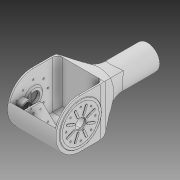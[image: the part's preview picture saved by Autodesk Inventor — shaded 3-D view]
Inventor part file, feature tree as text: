
AUTODESK INVENTOR PART (.ipt)
format: ipt  version: 2020 (Build 240168000, 168)  size: 957,952 bytes
history: native  units: mm
features: sketch x33, extrude x29, projected_geometry x8, plane x6, chamfer x3, fillet x3, pattern_circular x2, revolve x2, loft x2, other x2
ambient origin geometry x8: Origin, YZ Plane, XZ Plane, XY Plane, X Axis, Y Axis, Z Axis, Center Point
bodies: Solid1 (feature_tree)
feature tree (90):
  extrude  "Extrusion1"  Depth=250.0mm
  extrude  "Extrusion2"  Depth=100.0mm TaperAngle=0.0deg
  extrude  "Extrusion3"  TaperAngle=0.0deg  [1 undecoded]
  extrude  "Extrusion4"  Depth=10.0mm
  extrude  "Extrusion5"  Depth=30.0mm
  pattern_circular  "Circular Pattern1"  Count=8 Angle=360.0deg
  plane  "Work Plane1"
  plane  "Work Plane2"
  extrude  "Extrusion6"  Depth=30.0mm
  extrude  "Extrusion7"  Depth=2.0mm
  extrude  "Extrusion8"  Depth=2.0mm
  extrude  "Extrusion9"  [1 undecoded]
  chamfer  "Chamfer1"  Distance=10.0mm
  extrude  "Extrusion13"  Depth=10.0mm TaperAngle=0.0deg
  extrude  "Extrusion14"  Depth=3.0mm TaperAngle=0.0deg
  extrude  "Extrusion15"  Depth=95.1mm
  extrude  "Extrusion16"  Depth=10.0mm
  extrude  "Extrusion17"  Depth=80.0mm
  extrude  "Extrusion18"  Depth=60.0mm
  extrude  "Extrusion19"  Depth=80.0mm TaperAngle=360.0deg
  extrude  "Extrusion20"  Depth=15.5mm TaperAngle=0.0deg
  fillet  "Fillet2"  Radius=22.1mm
  pattern_circular  "Circular Pattern2"  Count=8 Angle=360.0deg
  extrude  "Extrusion22"  Depth=10.0mm
  plane  "Work Plane3"
  revolve  "Revolution1"  [1 undecoded]
  revolve  "Revolution2"  [1 undecoded]
  plane  "Work Plane4"
  extrude  "Extrusion23"  Depth=5.2mm
  extrude  "Extrusion24"  Depth=5.0mm
  fillet  "Fillet3"  Radius=5.2mm
  loft  "Loft1"
  extrude  "Extrusion25"  Depth=10.0mm
  extrude  "Extrusion26"  Depth=10.0mm
  extrude  "Extrusion27"  Depth=10.0mm
  extrude  "Extrusion28"  Depth=10.0mm
  plane  "Work Plane5"
  extrude  "Extrusion29"  Depth=10.0mm
  extrude  "Extrusion30"  Depth=10.0mm TaperAngle=0.0deg
  extrude  "Extrusion31"  Depth=10.0mm
  sketch  "Sketch38"  dims[d109=2.5mm d110=5.2mm]
  plane  "Work Plane6"
  extrude  "Extrusion33"  Depth=10.0mm TaperAngle=0.0deg
  loft  "Loft2"
  fillet  "Fillet5"  Radius=10.0mm
  chamfer  "Chamfer4"  Distance=18.8mm
  extrude  "Extrusion34"  Depth=10.0mm TaperAngle=0.0deg
  chamfer  "Chamfer5"  Distance=6.0mm
  sketch  "Sketch1"  dims[d0=50.0mm d1=250.0mm]
  sketch  "Sketch2"  dims[d2=50.0mm d3=100.0mm d4=0.0mm]
  sketch  "Sketch4"  dims[d5=5.0mm d7=0.0mm d8=0.0mm]
  sketch  "Sketch5"  dims[d11=10.0mm d12=0.0mm d14=85.0mm]
  sketch  "Sketch7"  dims[d15=1.0mm d16=0.0mm d17=30.0mm]
  projected_geometry  "Projected Loop1"
  sketch  "Sketch8"  dims[d18=3.3mm]
  projected_geometry  "Projected Loop2"
  projected_geometry  "Projected Loop4"
  sketch  "Sketch9"  dims[d19=15.0mm d20=0.0mm d21=80.0mm d22=360.0deg]
  sketch  "Sketch10"  dims[d24=30.0mm d25=30.0mm]
  sketch  "Sketch14"  dims[d30=-3.0mm d31=2.0mm]
  sketch  "Sketch15"  dims[d32=2.0mm d33=2.0mm]
  sketch  "Sketch16"  dims[d34=31.5mm d35=0.0mm d36=-5.0mm d38=10.0mm d39=0.0mm]
  sketch  "Sketch17"  dims[d40=22.1mm d41=10.0mm d42=0.0mm]
  sketch  "Sketch18"  dims[d43=5.0mm d44=3.0mm d45=0.0mm]
  sketch  "Sketch19"  dims[d56=3.0mm d57=2.0mm d58=45.0deg d62=95.1mm]
  sketch  "Sketch20"  dims[d63=10.0mm d64=0.0mm d65=3.0mm]
  sketch  "Sketch21"  dims[d66=0.5mm d67=0.0mm d68=80.0mm]
  sketch  "Sketch23"  dims[d69=15.5mm d70=0.0mm d71=60.0mm]
  other  "Work Axis1"
  sketch  "Sketch24"  dims[d72=3.2mm d73=80.0mm d75=360.0deg]
  sketch  "Sketch25"  dims[d77=15.5mm d78=0.0mm d79=15.5mm d80=0.0mm d81=22.1mm]
  projected_geometry  "Projected Loop5"
  projected_geometry  "Projected Loop6"
  sketch  "Sketch26"  dims[d82=0.0mm d83=0.0mm]
  sketch  "Sketch27"  dims[d84=76.0mm]
  sketch  "Sketch28"  dims[d85=0.1mm d86=0.0mm]
  sketch  "Sketch29"  dims[d87=15.0mm]
  sketch  "Sketch30"  dims[d88=2.0mm]
  sketch  "Sketch31"  dims[d89=22.5mm]
  sketch  "Sketch32"  dims[d90=0.8mm d91=0.0mm]
  sketch  "Sketch33"  dims[d92=0.2mm d93=80.0mm d94=360.0deg]
  projected_geometry  "Projected Loop7"
  sketch  "Sketch34"  dims[d96=24.43461mm d97=10.0mm]
  sketch  "Sketch35"  dims[d104=25.0mm d105=16.1mm]
  sketch  "Sketch36"  dims[d106=96.8mm d107=0.0mm d108=0.0mm]
  projected_geometry  "Projected Loop8"
  projected_geometry  "Projected Loop9"
  sketch  "Sketch39"  dims[d111=1.0mm d112=5.0mm d113=5.2mm]
  other  "Edges1"
  sketch  "Sketch40"  dims[d114=90.0deg d115=15.0mm d116=25.0mm d117=25.0mm d118=19.0mm d119=19.0mm d120=2.7mm d122=3.0mm d123=0.0mm d124=5.5mm d125=2.0mm d126=0.0mm d127=90.0deg d128=10.0mm d129=18.8mm d130=0.0mm d131=111.25mm d132=0.0mm d133=6.0mm d134=4.0mm d135=0.0mm d136=1.0mm d137=1.0mm d138=0.0mm d139=-7.0mm d140=1.0mm d141=1.0mm d142=0.0mm d143=7.0mm d144=5.0mm d145=6.0mm d146=0.0mm d147=90.0deg d148=0.0mm d149=90.0deg d150=0.0mm d151=0.0mm d152=27.0mm d153=0.0mm d154=4.712389mm d161=140.0mm d162=50.0mm d163=90.0mm d164=0.0mm d165=0.0mm d166=90.0deg d167=0.0mm d168=90.0deg d169=30.0mm d170=10.0mm d171=50.0mm d172=1.0mm d173=2.0mm d174=45.0deg d175=10.0mm d176=30.0mm d177=0.0mm d178=1.0mm d179=2.0mm d180=45.0deg d181=50.0mm d182=8.5mm]
note: 4 required parameter values undecoded (feature->parameter linkage not recoverable at this tier; creation-order binding heuristic only, values carry confidence <= 0.55)